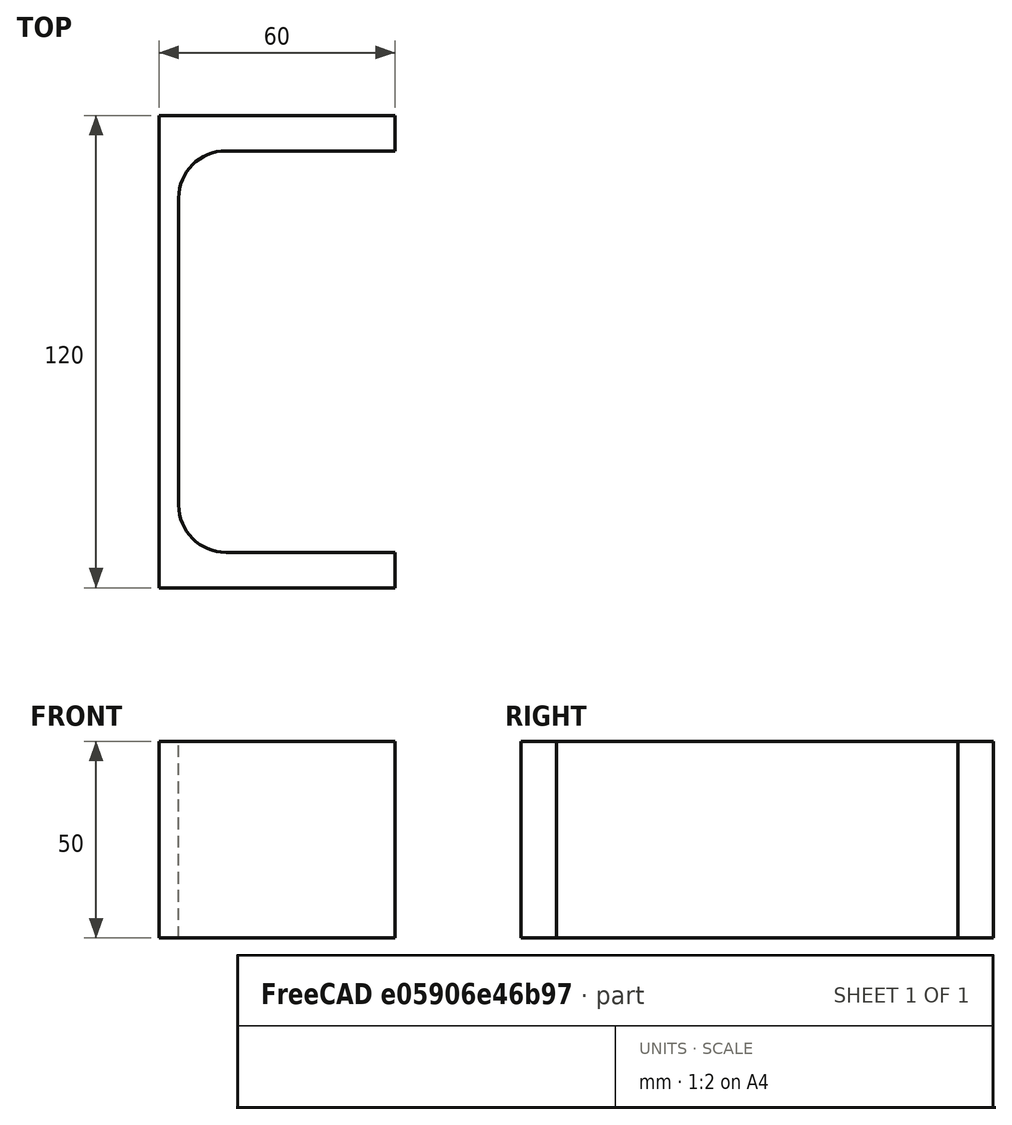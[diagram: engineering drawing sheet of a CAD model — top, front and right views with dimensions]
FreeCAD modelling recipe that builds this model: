
FCSTD DOCUMENT  (FreeCAD 0.20R29410 (Git))
Label: UPE-Profile 140 DIN1026-2 S235JR
License: All rights reserved
LicenseURL: http://en.wikipedia.org/wiki/All_rights_reserved
objects: Sketcher::SketchObject×1, Part::Extrusion×1
note: 2 computed .brp shape members not serialized (recipe doc carries the construction recipe); baked Part::Feature solids carry a one-line shape summary decoded from their .brp

FEATURE [Sketcher::SketchObject] Sketch
  FullyConstrained = true
  MapMode = 5
  sketch-geometry (10):
    g0: LineSegment StartX=5 StartY=-39 StartZ=0 EndX=5 EndY=39 EndZ=0
    g1: LineSegment StartX=17 StartY=51 StartZ=0 EndX=60 EndY=51 EndZ=0
    g2: LineSegment StartX=60 StartY=51 StartZ=0 EndX=60 EndY=60 EndZ=0
    g3: LineSegment StartX=60 StartY=-60 StartZ=0 EndX=60 EndY=-51 EndZ=0
    g4: LineSegment StartX=60 StartY=-51 StartZ=0 EndX=17 EndY=-51 EndZ=0
    g5: ArcOfCircle CenterX=17 CenterY=39 CenterZ=0 NormalX=0 NormalY=0 NormalZ=1 AngleXU=0 Radius=12 StartAngle=1.5708 EndAngle=3.14159
    g6: ArcOfCircle CenterX=17 CenterY=-39 CenterZ=0 NormalX=0 NormalY=0 NormalZ=1 AngleXU=0 Radius=12 StartAngle=3.14159 EndAngle=4.71239
    g7: LineSegment StartX=60 StartY=-60 StartZ=0 EndX=0 EndY=-60 EndZ=0
    g8: LineSegment StartX=0 StartY=-60 StartZ=0 EndX=0 EndY=60 EndZ=0
    g9: LineSegment StartX=0 StartY=60 StartZ=0 EndX=60 EndY=60 EndZ=0
  constraints (27):
    c: Vertical(g0)
    c: Coincident(g2,g1)
    c: Vertical(g2)
    c: Vertical(g3)
    c: Coincident(g4,g3)
    c: Horizontal(g4)
    c: Tangent(g1,g5) = 1.5708
    c: Tangent(g0,g5) = 1.5708
    c: Tangent(g0,g6) = 1.5708
    c: Tangent(g4,g6) = 1.5708
    c: Symmetric(g2,g3,g-1)
    c: DistanceY(g2) = 9
    c: Radius(g5) = 12
    c: Coincident(g3,g7)
    c: PointOnObject(g7,g-2)
    c: Horizontal(g7)
    c: Coincident(g7,g8)
    c: PointOnObject(g8,g-2)
    c: Coincident(g8,g9)
    c: Coincident(g9,g2)
    c: Horizontal(g9)
    c: Distance(g-1,g0) = 5
    c: DistanceX(g9,g9) = 60
    c: Horizontal(g1)
    c: Equal(g3,g2)
    c: Equal(g5,g6)
    c: DistanceY(g3,g2) = 120
FEATURE [Part::Extrusion] Extrude  label="UPE-Profile 140 DIN1026-2 S235JR"
  Base = -> Sketch
  Dir = (0,0,50)
  DirMode = 0
  FaceMakerClass = Part::FaceMakerExtrusion
  LengthFwd = 0
  LengthRev = 0
  Solid = true
  Symmetric = false
